# Revit family: HansWeitzel_2513
name_source: partatom
category: Allgemeines Modell
revit_build: Autodesk Revit 2017 (Build: 20160225_1515(x64)
units: mm (PartAtom-declared; Revit-internal decimal feet)

## family parameters
Basisbauteil = Wand
Beim Laden mit Abzugskörper schneiden = Nein
Bemaßung runder Anschluss = Durchmesser verwenden
Gemeinsam genutzt = Nein
Immer vertikal = Ja
Kann Basisbauteil für Bewehrung sein = Nein
Raumberechnungspunkt = Nein
Teiletyp = Normal

## types (1)
- HansWeitzel_2513
    BIM = https://media.live.bim.site
    BIMSITE_PRODUCT_ID = 759455f9cb85bc10949abfc32dc33b2d70ab223b
    Beschreibung = HZ-Stoßverbinder BLF Graphit Formteil an Sollbruchstelle einkürzen
    Breite [mm] = 40
    Dekor = Graphit
    Farbton = grau
    GTIN = 4022023220919
    Gewicht unverpackt (netto) [kg] = 0.008
    HAN = 2513
    HeinzeBIM = https://www.heinze.de
    Hersteller = Hans Weitzel GmbH & Co. KG
    Höhe [mm] = 93
    Ist System = Nein
    Ist Zubehör = Nein
    Menge pro Verpackungseinheit = 10
    Profilart = Anschlussprofi
    Tiefe (mm) = 30
    Typname = HZ-Stoßverbinder BLF Graphit
    Wandmontage möglich = Ja
    Werkstoff = Polystyrol
    max. Betriebstemperatur (°C) = 90

## geometry (parser evidence)
native form markers: Sweep x5
no freeform markers — native parametric forms only
